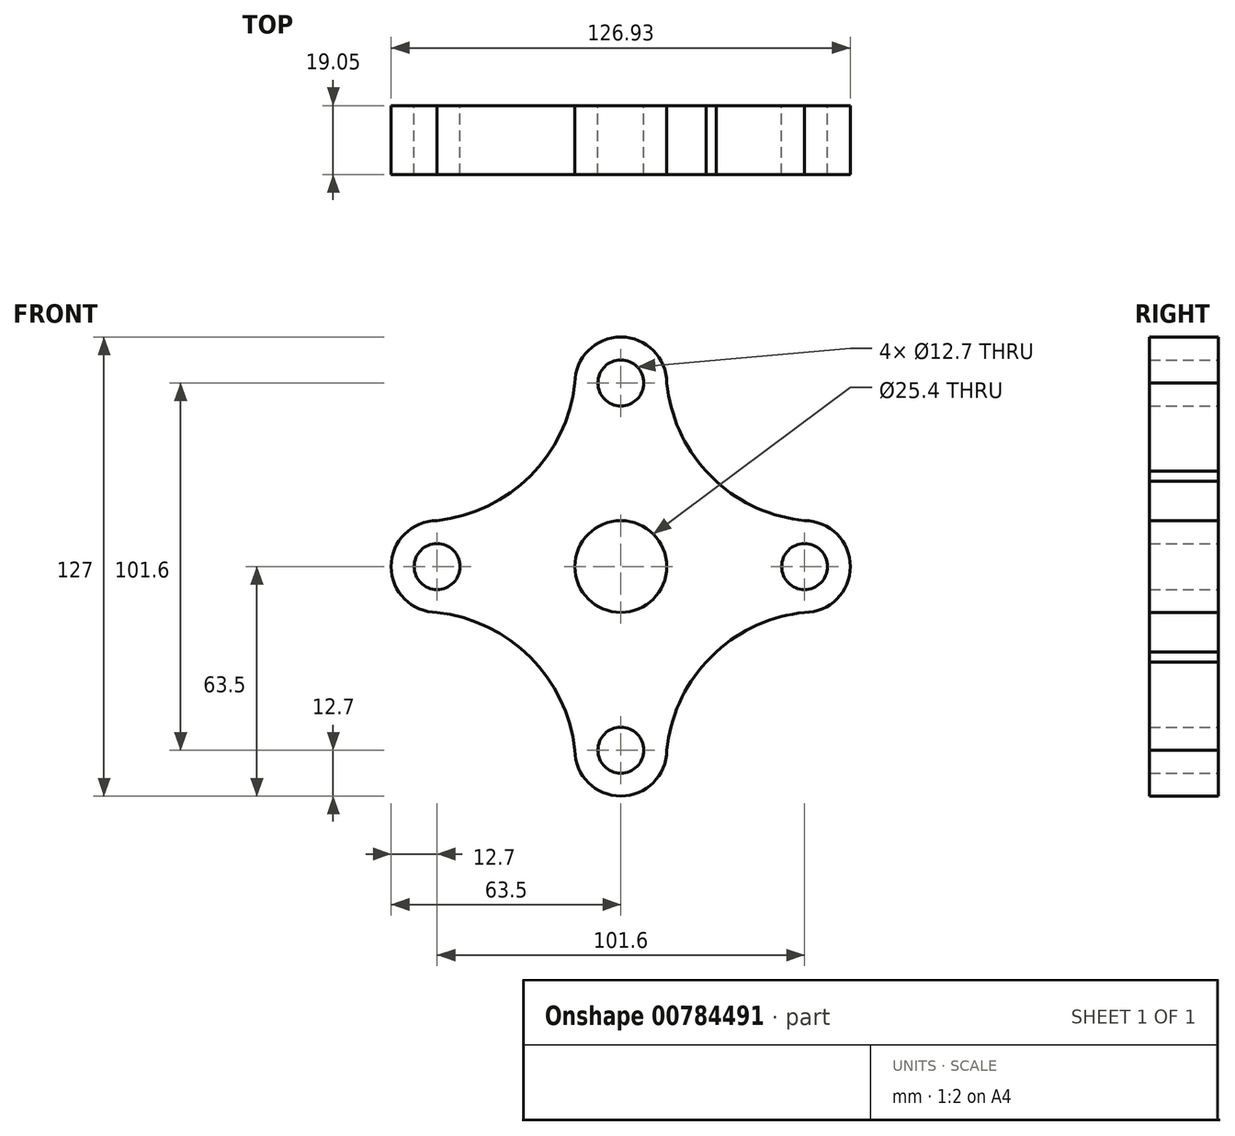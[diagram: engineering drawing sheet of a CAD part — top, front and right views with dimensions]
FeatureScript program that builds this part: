
annotation { "Feature Type Name" : "Feature", "Feature Type Description" : "" }
export const myFeature = defineFeature(function(context is Context, id is Id, definition is map)
    precondition{}
    {
        {
            var Q0;
            Q0=qCreatedBy(makeId("Front.planeOp"),FACE);
            var sketch = newSketch(context, id + "F0", { "sketchPlane" : qUnion([Q0])});
            skLineSegment(sketch, "E0", {"start": v(-50.8, 0) * mm, "end": v(-50.8, 0) * mm});
            skLineSegment(sketch, "E1", {"start": v(50.8, 0) * mm, "end": v(50.73, 0) * mm});
            skLineSegment(sketch, "E2", {"start": v(0, -50.8) * mm, "end": v(0, -12.7) * mm});
            skCircle(sketch, "E3", {"center": v(0, 50.8) * mm, "radius": 6.35 * mm});
            skCircle(sketch, "E4.MirrorC", {"center": v(0, -50.8) * mm, "radius": 6.35 * mm});
            skCircle(sketch, "E5", {"center": v(50.8, 0) * mm, "radius": 6.35 * mm});
            skCircle(sketch, "E6.MirrorC", {"center": v(-50.8, 0) * mm, "radius": 6.35 * mm});
            skCircle(sketch, "E7", {"center": v(0, 0) * mm, "radius": 12.7 * mm});
            skLineSegment(sketch, "E8", {"start": v(24.98, 24.98) * mm, "end": v(24.95, 24.95) * mm});
            skLineSegment(sketch, "E9", {"start": v(24.95, -24.95) * mm, "end": v(24.98, -24.98) * mm});
            skLineSegment(sketch, "E10.MirrorCS", {"start": v(26.39, -23.57) * mm, "end": v(23.57, -26.39) * mm});
            skLineSegment(sketch, "E11.MirrorCS", {"start": v(26.39, 23.57) * mm, "end": v(23.57, 26.39) * mm});
            skArc(sketch, "E12", {"start": v(12.7, 50.8) * mm, "mid": v(0, 63.5) * mm, "end": v(-12.7, 50.8) * mm});
            skArc(sketch, "E13", {"start": v(-50.8, 12.7) * mm, "mid": v(-63.5, 0) * mm, "end": v(-50.8, -12.7) * mm});
            skArc(sketch, "E14", {"start": v(50.8, -12.7) * mm, "mid": v(63.43, 0) * mm, "end": v(50.8, 12.7) * mm});
            skArc(sketch, "E15.MirrorCS", {"start": v(12.7, -50.8) * mm, "mid": v(0, -63.5) * mm, "end": v(-12.7, -50.8) * mm});
            skArc(sketch, "E16", {"start": v(-50.8, 12.7) * mm, "mid": v(-25.07, 25.07) * mm, "end": v(-12.7, 50.8) * mm});
            skArc(sketch, "E17", {"start": v(12.7, 50.8) * mm, "mid": v(24.95, 24.95) * mm, "end": v(50.8, 12.7) * mm});
            skArc(sketch, "E18.MirrorCS", {"start": v(-50.8, -12.7) * mm, "mid": v(-25.07, -25.07) * mm, "end": v(-12.7, -50.8) * mm});
            skArc(sketch, "E19.MirrorCS", {"start": v(12.7, -50.8) * mm, "mid": v(24.95, -24.95) * mm, "end": v(50.8, -12.7) * mm});
            skPoint(sketch, "E20.orphan", {"position": v(-63.5, 63.5) * mm});
            skPoint(sketch, "E21.end.orphan", {"position": v(56.21, 63.5) * mm});
            skPoint(sketch, "E22.orphan", {"position": v(-50.8, 50.8) * mm});
            skPoint(sketch, "E23.end.orphan", {"position": v(-63.5, -50.63) * mm});
            skPoint(sketch, "E23.start.orphan", {"position": v(-63.5, 50.8) * mm});
            skPoint(sketch, "E24.orphan", {"position": v(-56.65, 12.7) * mm});
            skPoint(sketch, "E25.orphan", {"position": v(-56.65, -12.7) * mm});
            skPoint(sketch, "E26.orphan", {"position": v(-30.4, 19.57) * mm});
            skPoint(sketch, "E27.MirrorCS.end.orphan", {"position": v(-20.07, 29.9) * mm});
            skLineSegment(sketch, "E28.trimOffspring", {"start": v(-24.98, -24.98) * mm, "end": v(-25.07, -25.07) * mm});
            skPoint(sketch, "E29.MirrorCS.end.orphan", {"position": v(-12.7, -50.8) * mm});
            skPoint(sketch, "E30.end.orphan", {"position": v(55.25, 12.7) * mm});
            skPoint(sketch, "E31.orphan", {"position": v(55.25, -12.7) * mm});
            skPoint(sketch, "E32.orphan", {"position": v(-30.4, -19.57) * mm});
            skPoint(sketch, "E33.end.orphan", {"position": v(-20.07, -29.9) * mm});
            skPoint(sketch, "E34.orphan", {"position": v(56.21, -63.5) * mm});
            skPoint(sketch, "E35.MirrorCS.start.orphan", {"position": v(-63.5, -63.5) * mm});
            skSolve(sketch);
        }
        {
            var Q0;
            Q0 = qSketchRegion(id + "F0", true);
            extrude(context, id + "F1", {"entities" : qUnion([Q0]), "depth" : 19.05 * mm, "offsetDistance" : 25.4 * mm});
        }
    });
